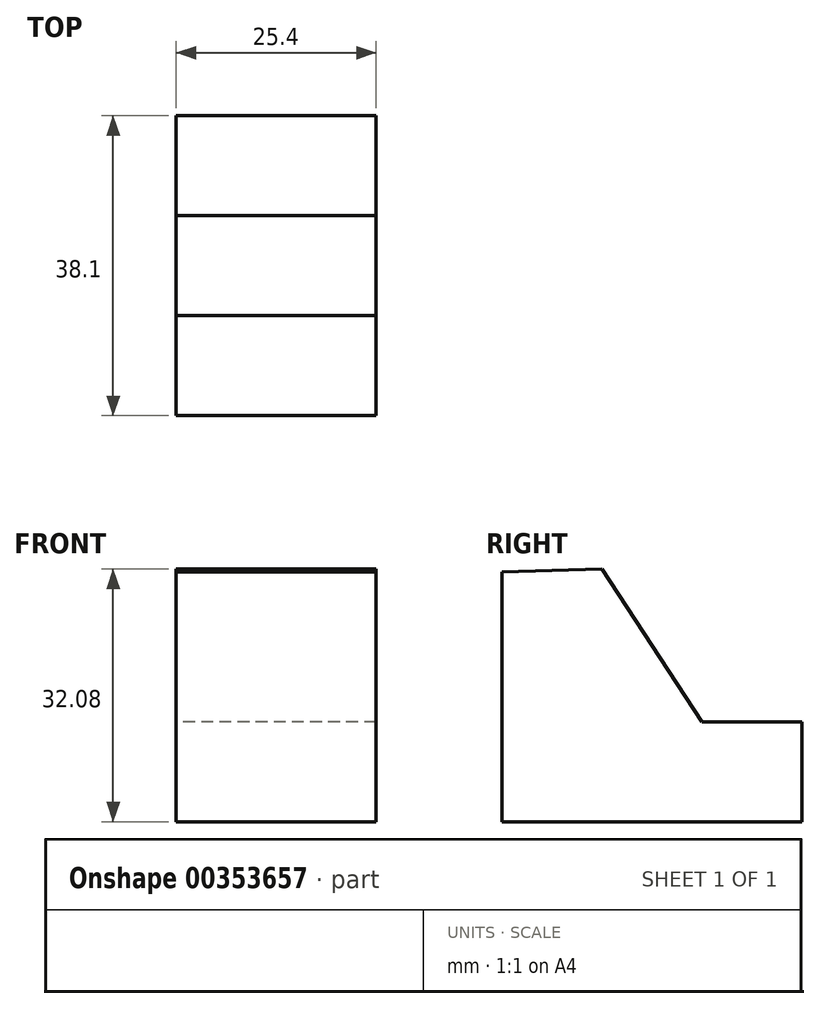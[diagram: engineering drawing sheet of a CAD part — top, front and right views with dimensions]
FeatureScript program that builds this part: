
annotation { "Feature Type Name" : "Feature", "Feature Type Description" : "" }
export const myFeature = defineFeature(function(context is Context, id is Id, definition is map)
    precondition{}
    {
        {
            var Q0;
            Q0=qCreatedBy(makeId("Right.planeOp"),FACE);
            var sketch = newSketch(context, id + "F0", { "sketchPlane" : qUnion([Q0])});
            skLineSegment(sketch, "E0", {"start": v(0, 31.75) * mm, "end": v(0, 0) * mm});
            skLineSegment(sketch, "E1", {"start": v(0, 0) * mm, "end": v(38.1, 0) * mm});
            skLineSegment(sketch, "E2", {"start": v(38.1, 0) * mm, "end": v(38.1, 12.7) * mm});
            skLineSegment(sketch, "E3", {"start": v(38.1, 12.7) * mm, "end": v(25.4, 12.7) * mm});
            skLineSegment(sketch, "E4", {"start": v(25.4, 12.7) * mm, "end": v(12.7, 32.08) * mm});
            skLineSegment(sketch, "E5", {"start": v(12.7, 32.08) * mm, "end": v(0, 31.75) * mm});
            skSolve(sketch);
        }
        {
            var Q0;
            Q0=makeQuery(id+"F0.imprint","IMPRINT",FACE,{"disambiguationData":[TD([[makeQuery(id+"F0.imprint","IMPRINT",EDGE,{"derivedFrom":sQuery(id+"F0.wireOp",EDGE,"E0")}),1.0]])]});
            extrude(context, id + "F1", {"entities" : qUnion([Q0]), "depth" : 25.4 * mm});
        }
    });
